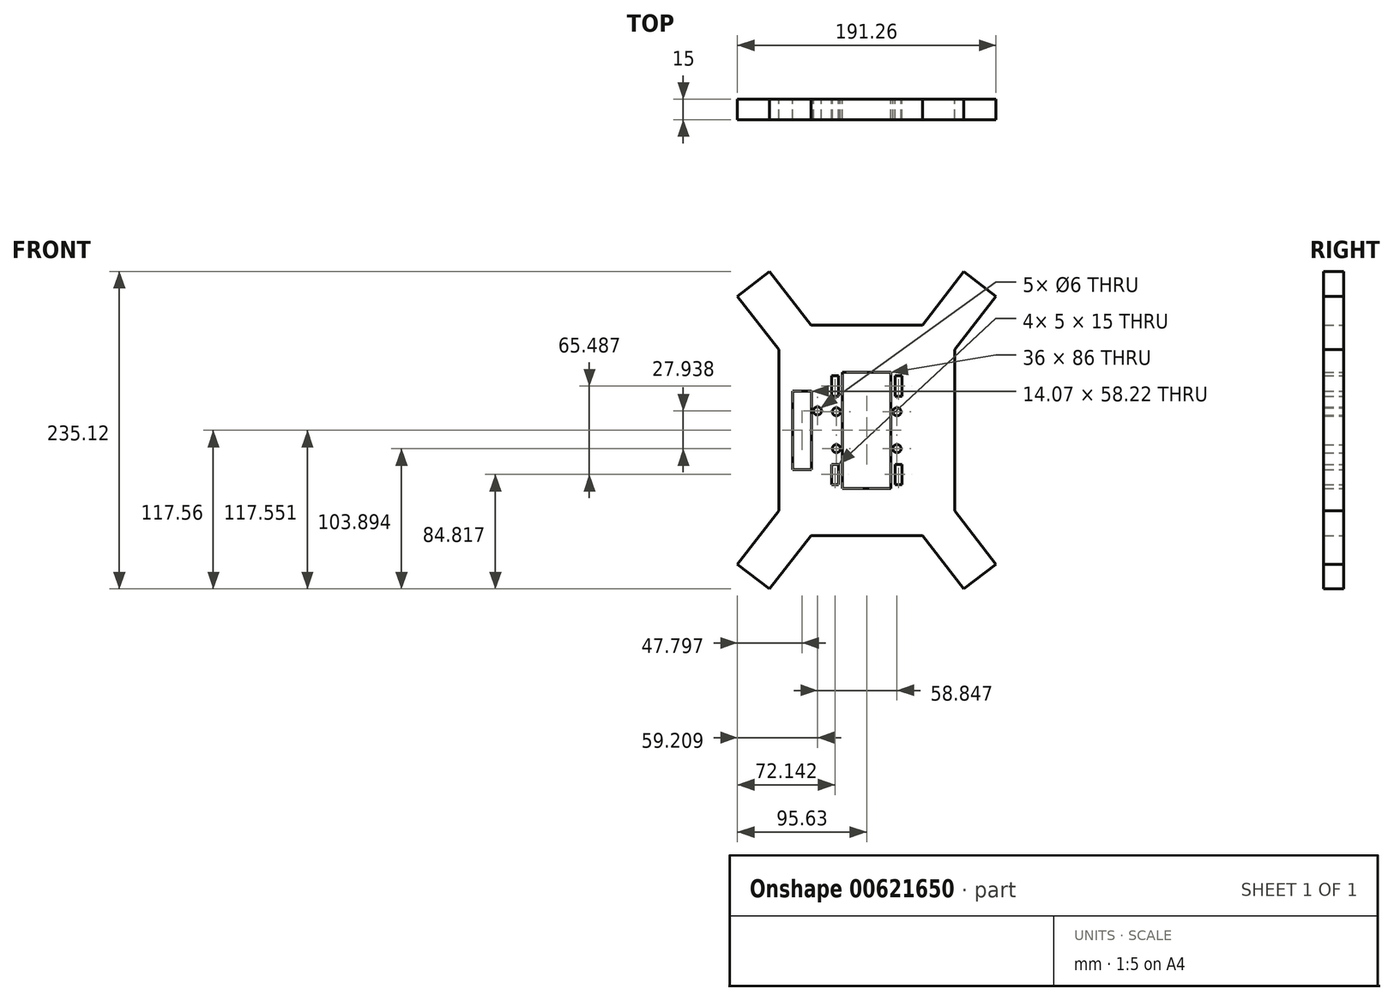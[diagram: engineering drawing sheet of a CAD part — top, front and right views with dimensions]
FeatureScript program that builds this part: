
annotation { "Feature Type Name" : "Feature", "Feature Type Description" : "" }
export const myFeature = defineFeature(function(context is Context, id is Id, definition is map)
    precondition{}
    {
        {
            var Q0;
            Q0=qCreatedBy(makeId("Front.planeOp"),FACE);
            var sketch = newSketch(context, id + "F0", { "sketchPlane" : qUnion([Q0])});
            skLineSegment(sketch, "E0", {"start": v(0, 22) * mm, "end": v(17, 22) * mm});
            skLineSegment(sketch, "E1", {"start": v(17, 22) * mm, "end": v(17, -22) * mm});
            skLineSegment(sketch, "E2", {"start": v(17, -22) * mm, "end": v(0, -22) * mm});
            skLineSegment(sketch, "E3.MirrorCS", {"start": v(-17, 22) * mm, "end": v(-17, -22) * mm});
            skLineSegment(sketch, "E4", {"start": v(-17, 22) * mm, "end": v(0, 22) * mm});
            skLineSegment(sketch, "E5", {"start": v(-17, -22) * mm, "end": v(0, -22) * mm});
            skLineSegment(sketch, "E6", {"start": v(214, 276.95) * mm, "end": v(-214, -276.95) * mm, "construction": true});
            skLineSegment(sketch, "E7", {"start": v(-214, 276.95) * mm, "end": v(214, -276.95) * mm, "construction": true});
            skCircle(sketch, "E8", {"center": v(214, -276.95) * mm, "radius": 120 * mm});
            skCircle(sketch, "E9.MirrorC", {"center": v(-214, -276.95) * mm, "radius": 120 * mm});
            skCircle(sketch, "E10.MirrorC", {"center": v(214, 276.95) * mm, "radius": 120 * mm});
            skCircle(sketch, "E11.MirrorC", {"center": v(-214, 276.95) * mm, "radius": 120 * mm});
            skCircle(sketch, "E12", {"center": v(22.43, 13.67) * mm, "radius": 3 * mm});
            skCircle(sketch, "E13.MirrorC", {"center": v(22.43, -13.67) * mm, "radius": 3 * mm});
            skCircle(sketch, "E14.MirrorC", {"center": v(-22.43, 13.67) * mm, "radius": 3 * mm});
            skCircle(sketch, "E15.MirrorC", {"center": v(-22.43, -13.67) * mm, "radius": 3 * mm});
            skLineSegment(sketch, "E16", {"start": v(0, -43) * mm, "end": v(18, -43) * mm});
            skLineSegment(sketch, "E17", {"start": v(18, -43) * mm, "end": v(18, 0) * mm});
            skLineSegment(sketch, "E18.MirrorCS", {"start": v(18, 43) * mm, "end": v(18, 0) * mm});
            skLineSegment(sketch, "E19.MirrorCS", {"start": v(0, 43) * mm, "end": v(18, 43) * mm});
            skLineSegment(sketch, "E20.MirrorCS", {"start": v(-18, 43) * mm, "end": v(-18, 0) * mm});
            skLineSegment(sketch, "E21.MirrorCS", {"start": v(0, 43) * mm, "end": v(-18, 43) * mm});
            skLineSegment(sketch, "E22.MirrorCS", {"start": v(0, -43) * mm, "end": v(-18, -43) * mm});
            skLineSegment(sketch, "E23.MirrorCS", {"start": v(-18, -43) * mm, "end": v(-18, 0) * mm});
            skLineSegment(sketch, "E24.bottom", {"start": v(20.99, 40.24) * mm, "end": v(25.99, 40.24) * mm});
            skLineSegment(sketch, "E24.top", {"start": v(20.99, 25.24) * mm, "end": v(25.99, 25.24) * mm});
            skLineSegment(sketch, "E24.left", {"start": v(20.99, 40.24) * mm, "end": v(20.99, 25.24) * mm});
            skLineSegment(sketch, "E24.right", {"start": v(25.99, 40.24) * mm, "end": v(25.99, 25.24) * mm});
            skLineSegment(sketch, "E25.MirrorCS", {"start": v(-20.99, 40.24) * mm, "end": v(-25.99, 40.24) * mm});
            skLineSegment(sketch, "E26.MirrorCS", {"start": v(-25.99, 40.24) * mm, "end": v(-25.99, 25.24) * mm});
            skLineSegment(sketch, "E27.MirrorCS", {"start": v(-20.99, 25.24) * mm, "end": v(-25.99, 25.24) * mm});
            skLineSegment(sketch, "E28.MirrorCS", {"start": v(-20.99, 40.24) * mm, "end": v(-20.99, 25.24) * mm});
            skLineSegment(sketch, "E29", {"start": v(0, 0) * mm, "end": v(71.76, 0) * mm, "construction": true});
            skLineSegment(sketch, "E30.MirrorCS", {"start": v(25.99, -40.24) * mm, "end": v(25.99, -25.24) * mm});
            skLineSegment(sketch, "E31.MirrorCS", {"start": v(20.99, -40.24) * mm, "end": v(25.99, -40.24) * mm});
            skLineSegment(sketch, "E32.MirrorCS", {"start": v(20.99, -25.24) * mm, "end": v(25.99, -25.24) * mm});
            skLineSegment(sketch, "E33.MirrorCS", {"start": v(20.99, -40.24) * mm, "end": v(20.99, -25.24) * mm});
            skLineSegment(sketch, "E34.MirrorCS", {"start": v(-20.99, -40.24) * mm, "end": v(-20.99, -25.24) * mm});
            skLineSegment(sketch, "E35.MirrorCS", {"start": v(-20.99, -40.24) * mm, "end": v(-25.99, -40.24) * mm});
            skLineSegment(sketch, "E36.MirrorCS", {"start": v(-25.99, -40.24) * mm, "end": v(-25.99, -25.24) * mm});
            skLineSegment(sketch, "E37.MirrorCS", {"start": v(-20.99, -25.24) * mm, "end": v(-25.99, -25.24) * mm});
            skLineSegment(sketch, "E38.bottom", {"start": v(-54.87, 29.1) * mm, "end": v(-40.8, 29.1) * mm});
            skLineSegment(sketch, "E38.top", {"start": v(-54.87, -29.12) * mm, "end": v(-40.8, -29.12) * mm});
            skLineSegment(sketch, "E38.left", {"start": v(-54.87, 29.1) * mm, "end": v(-54.87, -29.12) * mm});
            skLineSegment(sketch, "E38.right", {"start": v(-40.8, 29.1) * mm, "end": v(-40.8, -29.12) * mm});
            skLineSegment(sketch, "E39.MirrorCS", {"start": v(-54.87, -29.1) * mm, "end": v(-40.8, -29.1) * mm});
            skLineSegment(sketch, "E40.MirrorCS", {"start": v(-54.87, 29.12) * mm, "end": v(-40.8, 29.12) * mm});
            skLineSegment(sketch, "E41", {"start": v(-54.87, 29.12) * mm, "end": v(-40.8, -29.1) * mm, "construction": true});
            skLineSegment(sketch, "E42", {"start": v(-40.8, 29.12) * mm, "end": v(-54.87, -29.1) * mm, "construction": true});
            skCircle(sketch, "E43", {"center": v(-36.42, 14.27) * mm, "radius": 3 * mm});
            skLineSegment(sketch, "E44", {"start": v(0, 0) * mm, "end": v(0, 95.93) * mm, "construction": true});
            skLineSegment(sketch, "E45", {"start": v(0, 78) * mm, "end": v(41.32, 78) * mm});
            skLineSegment(sketch, "E46", {"start": v(41.32, 78) * mm, "end": v(71.89, 117.56) * mm});
            skLineSegment(sketch, "E47", {"start": v(71.89, 117.56) * mm, "end": v(83.76, 108.4) * mm});
            skLineSegment(sketch, "E48.MirrorCS", {"start": v(95.63, 99.22) * mm, "end": v(83.76, 108.4) * mm});
            skLineSegment(sketch, "E49.MirrorCS", {"start": v(65.05, 59.66) * mm, "end": v(95.63, 99.22) * mm});
            skLineSegment(sketch, "E50.MirrorCS", {"start": v(0, 78) * mm, "end": v(-41.32, 78) * mm});
            skLineSegment(sketch, "E51.MirrorCS", {"start": v(-41.32, 78) * mm, "end": v(-71.89, 117.56) * mm});
            skLineSegment(sketch, "E52.MirrorCS", {"start": v(-71.89, 117.56) * mm, "end": v(-83.76, 108.4) * mm});
            skLineSegment(sketch, "E53.MirrorCS", {"start": v(-95.63, 99.22) * mm, "end": v(-83.76, 108.4) * mm});
            skLineSegment(sketch, "E54.MirrorCS", {"start": v(-65.05, 59.66) * mm, "end": v(-95.63, 99.22) * mm});
            skLineSegment(sketch, "E55.MirrorCS", {"start": v(65.05, -59.66) * mm, "end": v(95.63, -99.22) * mm});
            skLineSegment(sketch, "E56.MirrorCS", {"start": v(95.63, -99.22) * mm, "end": v(83.76, -108.4) * mm});
            skLineSegment(sketch, "E57.MirrorCS", {"start": v(71.89, -117.56) * mm, "end": v(83.76, -108.4) * mm});
            skLineSegment(sketch, "E58.MirrorCS", {"start": v(41.32, -78) * mm, "end": v(71.89, -117.56) * mm});
            skLineSegment(sketch, "E59.MirrorCS", {"start": v(0, -78) * mm, "end": v(41.32, -78) * mm});
            skLineSegment(sketch, "E60.MirrorCS", {"start": v(0, -78) * mm, "end": v(-41.32, -78) * mm});
            skLineSegment(sketch, "E61.MirrorCS", {"start": v(-41.32, -78) * mm, "end": v(-71.89, -117.56) * mm});
            skLineSegment(sketch, "E62.MirrorCS", {"start": v(-65.05, -59.66) * mm, "end": v(-95.63, -99.22) * mm});
            skLineSegment(sketch, "E63.MirrorCS", {"start": v(-71.89, -117.56) * mm, "end": v(-83.76, -108.4) * mm});
            skLineSegment(sketch, "E64.MirrorCS", {"start": v(-95.63, -99.22) * mm, "end": v(-83.76, -108.4) * mm});
            skLineSegment(sketch, "E65", {"start": v(65.05, -59.66) * mm, "end": v(65.05, 59.66) * mm});
            skLineSegment(sketch, "E66", {"start": v(-65.05, -59.66) * mm, "end": v(-65.05, 59.66) * mm});
            skSolve(sketch);
        }
        {
            var Q0;
            Q0=makeQuery(id+"F0.imprint","IMPRINT",FACE,{"disambiguationData":[TD([[makeQuery(id+"F0.imprint","IMPRINT",EDGE,{"derivedFrom":sQuery(id+"F0.wireOp",EDGE,"E12")}),-1.0]])]});
            extrude(context, id + "F1", {"entities" : qUnion([Q0]), "depth" : 15 * mm, "offsetDistance" : 25 * mm});
        }
    });
